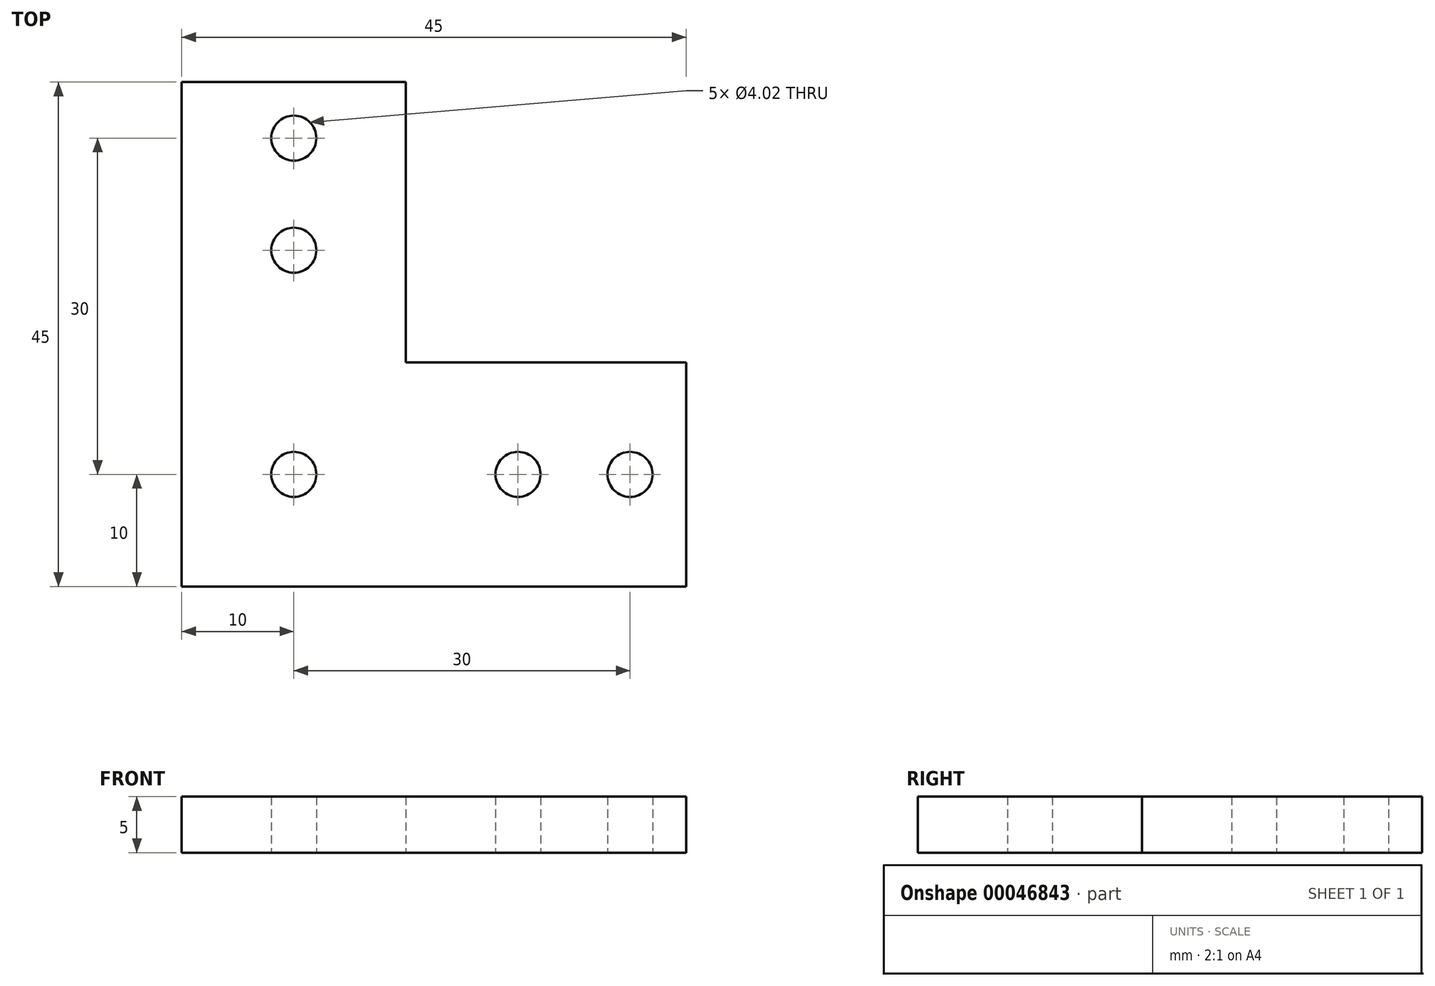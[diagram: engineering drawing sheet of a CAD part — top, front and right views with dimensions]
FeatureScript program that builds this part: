
annotation { "Feature Type Name" : "Feature", "Feature Type Description" : "" }
export const myFeature = defineFeature(function(context is Context, id is Id, definition is map)
    precondition{}
    {
        {
            var Q0;
            Q0=qCreatedBy(makeId("Top.planeOp"),FACE);
            var sketch = newSketch(context, id + "F0", { "sketchPlane" : qUnion([Q0])});
            skLineSegment(sketch, "E0", {"start": v(0, 0) * mm, "end": v(0, 45) * mm});
            skLineSegment(sketch, "E1", {"start": v(0, 45) * mm, "end": v(20, 45) * mm});
            skLineSegment(sketch, "E2", {"start": v(20, 45) * mm, "end": v(20, 20) * mm});
            skLineSegment(sketch, "E3", {"start": v(20, 20) * mm, "end": v(45, 20) * mm});
            skLineSegment(sketch, "E4", {"start": v(45, 20) * mm, "end": v(45, 0) * mm});
            skLineSegment(sketch, "E5", {"start": v(45, 0) * mm, "end": v(0, 0) * mm});
            skCircle(sketch, "E6", {"center": v(10, 10) * mm, "radius": 2 * mm});
            skCircle(sketch, "E7", {"center": v(30, 10) * mm, "radius": 2 * mm});
            skCircle(sketch, "E8", {"center": v(40, 10) * mm, "radius": 2 * mm});
            skCircle(sketch, "E9", {"center": v(10, 40) * mm, "radius": 2 * mm});
            skCircle(sketch, "E10", {"center": v(10, 30) * mm, "radius": 2 * mm});
            skSolve(sketch);
        }
        {
            var Q0;
            Q0 = qSketchRegion(id + "F0", true);
            extrude(context, id + "F1", {"entities" : qUnion([Q0]), "depth" : 5 * mm});
        }
    });
